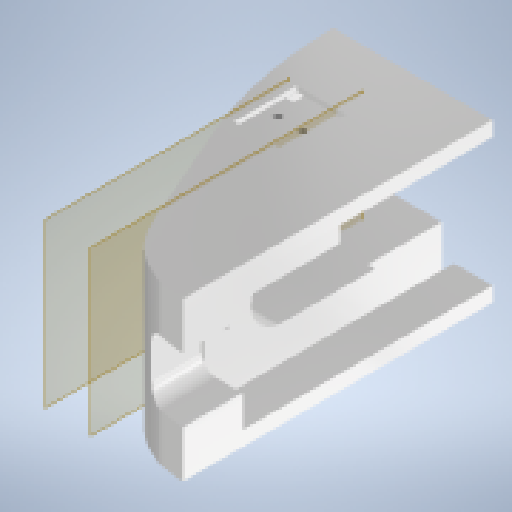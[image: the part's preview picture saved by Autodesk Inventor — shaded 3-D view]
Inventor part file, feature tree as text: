
AUTODESK INVENTOR PART (.ipt)
format: ipt  version: 2025 (Build 290162010, 162A)  size: 391,168 bytes
history: native  units: mm
features: extrude x8, sketch x7, other x4, hole x3, fillet x3, plane x2, reference x2
ambient origin geometry x8: Origin, YZ Plane, XZ Plane, XY Plane, X Axis, Y Axis, Z Axis, Center Point
bodies: Volumenkörper1 (feature_tree)
feature tree (29):
  sketch  "Skizze1"  dims[d0=5.0mm d1=45.0mm d2=30.0mm d3=0.0mm]
  extrude  "Extrusion1"  Depth=30.0mm TaperAngle=0.0deg
  hole  "Bohrung2"  [1 undecoded]
  extrude  "Extrusion2"  [1 undecoded]
  plane  "Arbeitsebene1"
  hole  "Bohrung4"  [1 undecoded]
  extrude  "Extrusion3"  Depth=2.0mm
  plane  "Arbeitsebene2"
  hole  "Bohrung5"  [1 undecoded]
  extrude  "Extrusion4"  Depth=2.0mm
  extrude  "Extrusion5"  Depth=2.0mm TaperAngle=0.0deg
  extrude  "Extrusion6"  [1 undecoded]
  fillet  "Rundung2"  Radius=7.8mm
  sketch  "Skizze13"  dims[d41=12.0mm d42=0.0mm d43=0.0mm d44=3.2mm d45=6.0mm d46=6.3mm d47=2.0mm d48=90.0deg d49=8.0mm d50=20.594885mm d51=12.0mm d52=8.0mm d53=0.0mm d54=-19.5mm d56=7.8mm d57=1.0mm d58=0.0mm d59=2.0mm d60=0.0mm d61=12.0mm d62=8.5mm d63=0.0mm d65=0.5mm d66=3.0mm d67=1.0mm d68=0.0mm d69=8.5mm d70=0.0mm d71=3.0mm d72=15.0mm d73=15.0mm d75=35.0mm d76=2.0mm d77=0.0mm d78=2.0mm]
  extrude  "Extrusion7"  Depth=2.0mm TaperAngle=0.0deg
  extrude  "Extrusion8"  Depth=2.0mm TaperAngle=0.0deg
  fillet  "Rundung3"  Radius=12.0mm
  fillet  "Rundung4"  Radius=8.5mm
  reference  "Referenz1"
  sketch  "Skizze3"  dims[d4=15.0mm d14=6.5mm]
  reference  "Referenz3"
  sketch  "Skizze5"  dims[d15=5.0mm]
  sketch  "Skizze7"  dims[d16=1.567mm d17=8.0mm d18=4.0mm d19=2.0mm d20=90.0deg d21=10.0mm d22=20.594885mm d30=-10.0mm]
  sketch  "Skizze8"  dims[d31=15.0mm d32=15.0mm]
  sketch  "Skizze9"  dims[d33=3.2mm d34=6.0mm d35=6.3mm d36=2.0mm d37=90.0deg d38=8.0mm d39=20.594885mm d40=14.0mm]
  other  "<userpath>\GIT\HDVKBM\CAD\Krandemonstrator\Demonstrator.iam"
  other  "Demonstrator.iam"
  other  "Träger:1"
  other  "AS 1112 (2) - Metrisch M4  Typ 5:1"
note: 5 required parameter values undecoded (feature->parameter linkage not recoverable at this tier; creation-order binding heuristic only, values carry confidence <= 0.55)
